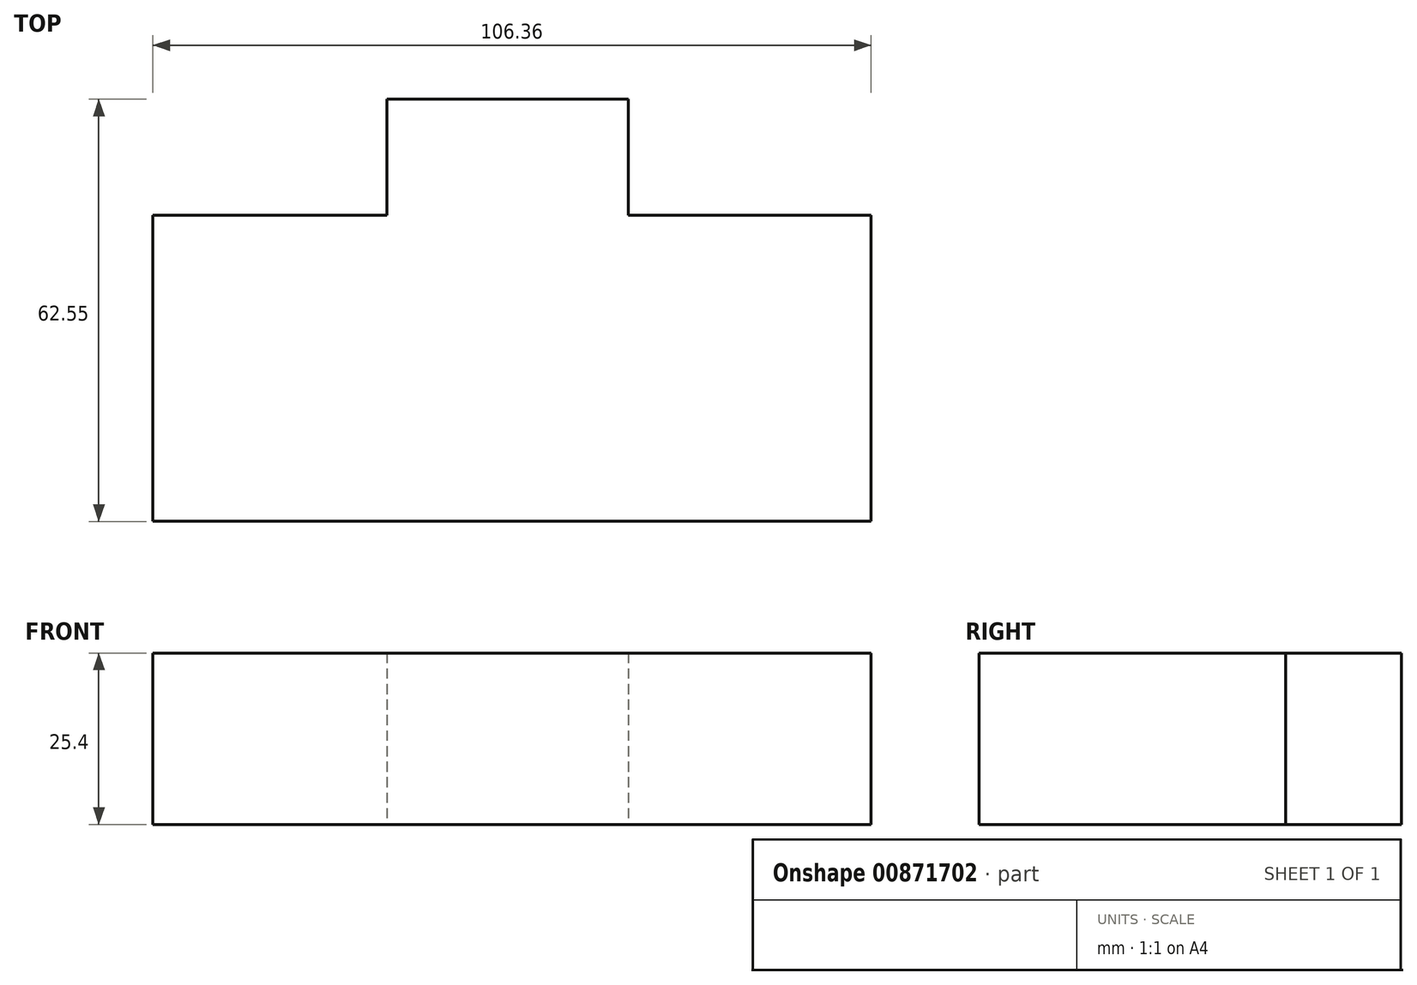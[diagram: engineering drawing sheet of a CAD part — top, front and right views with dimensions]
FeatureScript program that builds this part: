
annotation { "Feature Type Name" : "Feature", "Feature Type Description" : "" }
export const myFeature = defineFeature(function(context is Context, id is Id, definition is map)
    precondition{}
    {
        {
            var Q0;
            Q0=qCreatedBy(makeId("Top.planeOp"),FACE);
            var sketch = newSketch(context, id + "F0", { "sketchPlane" : qUnion([Q0])});
            skLineSegment(sketch, "E0.bottom", {"start": v(-52.97, -25.48) * mm, "end": v(53.39, -25.48) * mm});
            skLineSegment(sketch, "E0.left", {"start": v(-52.97, -25.48) * mm, "end": v(-52.97, 19.9) * mm});
            skLineSegment(sketch, "E0.right", {"start": v(53.39, -25.48) * mm, "end": v(53.39, 19.9) * mm});
            skLineSegment(sketch, "E1", {"start": v(-52.97, 19.9) * mm, "end": v(-18.32, 19.9) * mm});
            skLineSegment(sketch, "E2", {"start": v(-18.32, 19.9) * mm, "end": v(-18.32, 37.07) * mm});
            skLineSegment(sketch, "E3", {"start": v(-18.32, 37.07) * mm, "end": v(17.45, 37.07) * mm});
            skLineSegment(sketch, "E4", {"start": v(17.45, 37.07) * mm, "end": v(17.45, 19.9) * mm});
            skLineSegment(sketch, "E5", {"start": v(17.45, 19.9) * mm, "end": v(53.39, 19.9) * mm});
            skSolve(sketch);
        }
        {
            var Q0;
            Q0=makeQuery(id+"F0.imprint","IMPRINT",FACE,{"disambiguationData":[TD([[makeQuery(id+"F0.imprint","IMPRINT",EDGE,{"derivedFrom":sQuery(id+"F0.wireOp",EDGE,"E0.bottom")}),1.0]])]});
            extrude(context, id + "F1", {"entities" : qUnion([Q0]), "depth" : 25.4 * mm, "offsetDistance" : 25.4 * mm});
        }
    });
